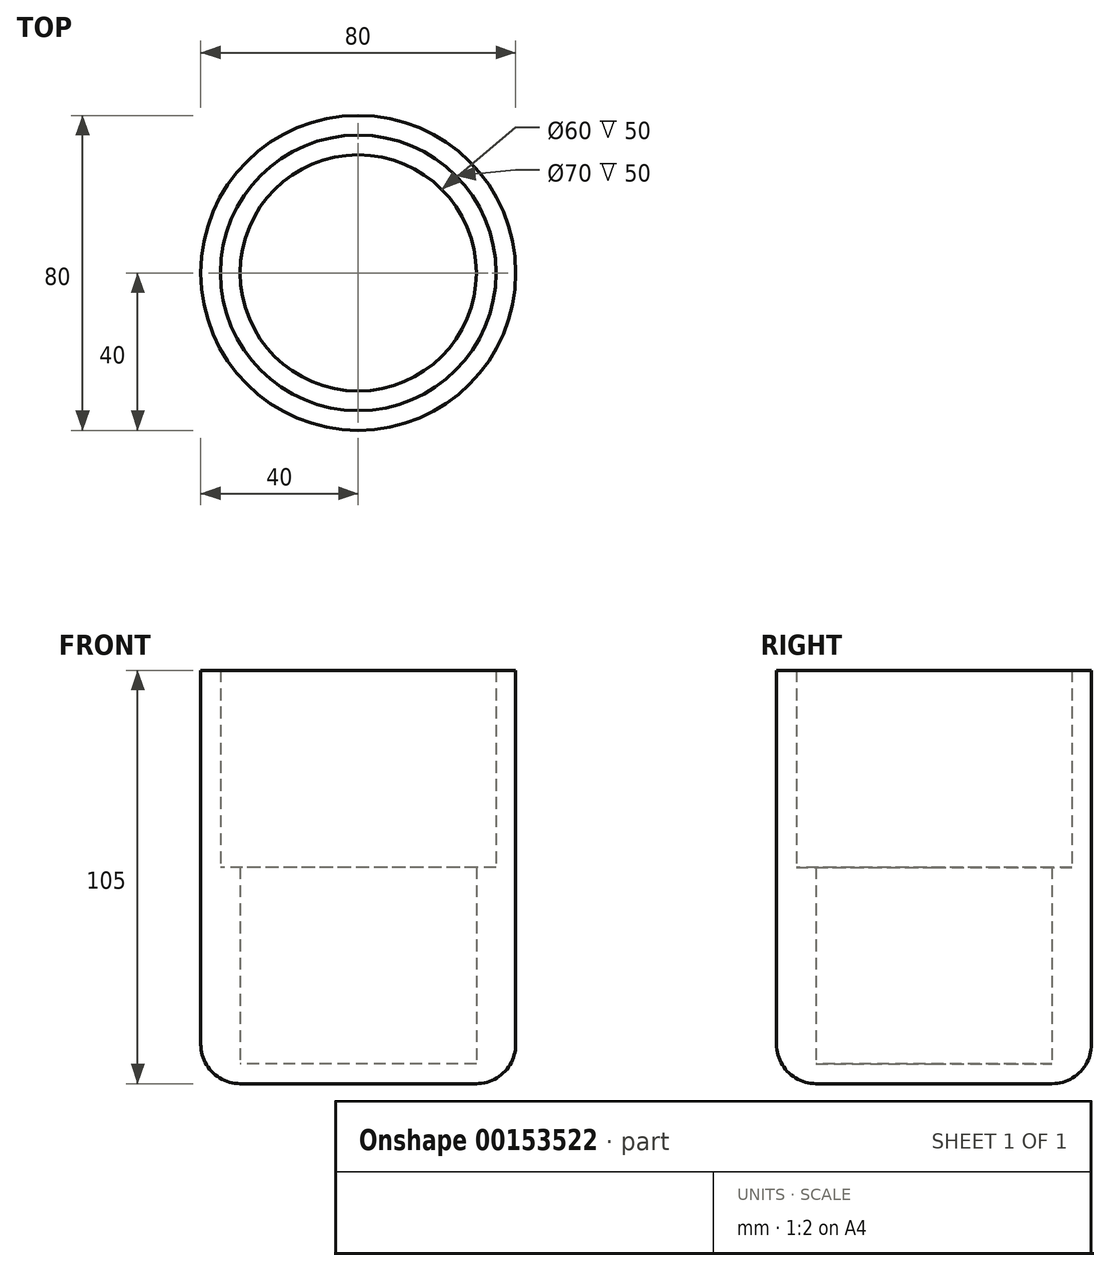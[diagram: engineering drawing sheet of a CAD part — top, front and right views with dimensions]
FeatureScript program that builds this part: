
annotation { "Feature Type Name" : "Feature", "Feature Type Description" : "" }
export const myFeature = defineFeature(function(context is Context, id is Id, definition is map)
    precondition{}
    {
        {
            var Q0;
            Q0=qCreatedBy(makeId("Top.planeOp"),FACE);
            var sketch = newSketch(context, id + "F0", { "sketchPlane" : qUnion([Q0])});
            skCircle(sketch, "E0", {"center": v(0, 0) * mm, "radius": 40 * mm});
            skCircle(sketch, "E1", {"center": v(0, 0) * mm, "radius": 35 * mm});
            skCircle(sketch, "E2", {"center": v(0, 0) * mm, "radius": 30 * mm});
            skSolve(sketch);
        }
        {
            var Q0;
            Q0 = qSketchRegion(id + "F0", true);
            var Q1;
            Q1=makeQuery(id+"F0.imprint","IMPRINT",FACE,{"disambiguationData":[TD([[makeQuery(id+"F0.imprint","IMPRINT",EDGE,{"derivedFrom":sQuery(id+"F0.wireOp",EDGE,"E1")}),1.0]])]});
            extrude(context, id + "F1", {"entities" : qUnion([Q0, Q1]), "depth" : 50 * mm});
        }
        {
            var Q0;
            Q0=makeQuery(id+"F0.imprint","IMPRINT",FACE,{"disambiguationData":[TD([[makeQuery(id+"F0.imprint","IMPRINT",EDGE,{"derivedFrom":sQuery(id+"F0.wireOp",EDGE,"E0")}),1.0]])]});
            extrude(context, id + "F2", {"entities" : qUnion([Q0]), "operationType" : NewBodyOperationType.ADD, "depth" : 100 * mm});
        }
        {
            var Q0;
            Q0=makeQuery(id+"F0.imprint","IMPRINT",FACE,{"disambiguationData":[TD([[makeQuery(id+"F0.imprint","IMPRINT",EDGE,{"derivedFrom":sQuery(id+"F0.wireOp",EDGE,"E2")}),1.0]])]});
            var Q1;
            Q1=makeQuery(id+"F0.imprint","IMPRINT",FACE,{"disambiguationData":[TD([[makeQuery(id+"F0.imprint","IMPRINT",EDGE,{"derivedFrom":sQuery(id+"F0.wireOp",EDGE,"E1")}),1.0]])]});
            var Q2;
            Q2=makeQuery(id+"F0.imprint","IMPRINT",FACE,{"disambiguationData":[TD([[makeQuery(id+"F0.imprint","IMPRINT",EDGE,{"derivedFrom":sQuery(id+"F0.wireOp",EDGE,"E0")}),1.0]])]});
            extrude(context, id + "F3", {"entities" : qUnion([Q0, Q1, Q2]), "operationType" : NewBodyOperationType.ADD, "oppositeDirection" : true, "depth" : 5 * mm});
        }
        {
            var Q0;
            Q0=makeQuery(id+"F3.opExtrude","CAP_EDGE",EDGE,{"disambiguationData":[OSD([sQuery(id+"F0.wireOp",EDGE,"E0")])],"isStart":false});
            fillet(context, id + "F4", {"entities" : qUnion([Q0]), "radius" : 10 * mm, "tangentPropagation" : true, "allowEdgeOverflow" : false});
        }
    });
